# Revit family: KDW030046
name_source: partatom
category: Plumbing Fixtures
revit_build: Autodesk Revit 2015 (Build: 20140606_1530(x64)
units: mm (PartAtom-declared; Revit-internal decimal feet)

## types (1)
- KDW030046
    Accessory = Yes
    Additional features of the object = https://www.kaldewei.co.uk
    BIMobject category = Basins
    Brand url = http://www.kaldewei.com
    Color = https://www.kaldewei.co.uk
    ColourOptions = https://www.kaldewei.co.uk
    Configurator link = https://www.kaldewei.co.uk
    Description details = KALDEWEI international Worldwide partner for iconic bathroom solutions made of KALDEWEI steel enamel  KALDEWEI steel enamel delivers unique advantages that inspire excellence in bathroom design. Projects across the world, from upmarket hotels to private homes, capture the sophisticated aesthetic that recommends KALDEWEI as the partner of choice. As a leading international manufacturer of high-quality shower surfaces, bathtubs and washbasins made of superior steel enamel, KALDEWEI today is present in more than 80 countries.
    Design country = Germany
    Durability = https://EN 14688
    Edition number = 1
    IFC Classification = Furnishing Element
    IfcExportAs = WASHHANDBASIN
    IfcExportType = IfcSanitaryTerminalType
    Link towards a photo of the product = https://www.kaldewei.co.uk
    Manufacturer country = Germany
    ManufacturerCountry = GERMANY
    ManufacturerName = KALDEWEI
    Material = steel enamel
    Material main = Steel
    Material secondary = Enamel
    NBS Reference Code = 35-65-70-94
    NBS Reference Description = Wash Basin Systems
    Name = MIENA bowl
    Nominal height = 450 cm
    Nominal width = 0 cm
    ObjectName = MIENA bowl ø 450
    ObjectNorm = EN 14688 EU DECLARATION OF PERFORMANCE (https://www.kaldewei.de
    Polantis code = KDW030046
    Product Guid = 65f3eec7-26ce-4da6-85c4-2e1fca35417f
    Product SKU = 3180
    Product certification = https://www.kaldewei.co.uk
    Product data url = http://bimobject.com
    Product family = MIENA
    Product group = Washbasin
    Product url = https://www.kaldewei.co.uk
    ProductInformation = Model No. 3180: The round bowls of the MIENA line appear filigree, almost fragile. The contours run in a single gentle and harmonious curve towards the waste outlet. The resulting reduced footprint gives the bowls an even more weightless look. One almost has the sense that they are floating on the given undercounter.
    QR code = http://bimobject.com
    SerialNumber = 3180
    Shape = Bowl
    Size = ø 450
    Sound Insulation = DIN 4109:2016, VDI4100:2012
    Sustainability = https://EN 15804
    Technical data link = https://kaldewei.typo-live.web-factory.de
    Technical description = https://www.kaldewei.co.uk
    Type of accessories = https://www.kaldewei.co.uk
    Type of support framing = https://www.kaldewei.co.uk
    UNSPSC Code = 301815
    UNSPSCCode = 30181504
    UNSPSCNames = Sinks
    URL = https://www.kaldewei.com
    Uniclass 1.4 Code = L7212
    Uniclass 1.4 Description = Washbasins
    Uniclass 2.0 Code = SS-35-65-70-94
    Uniclass 2.0 Description = Wash Basin Systems
    Uniclass2 = Pr_40_20_96
    Version = 3
    WarrantyDurationParts = 30
    WarrantyDurationUnit = Year
    WarrantyStartDate = https://www.kaldewei.co.uk
    Website link = https://www.kaldewei.co.uk
    Weight = 7.4
    Weight Net (Kg) = 7.4

## geometry (parser evidence)
native form markers: Sweep x8
no freeform markers — native parametric forms only
